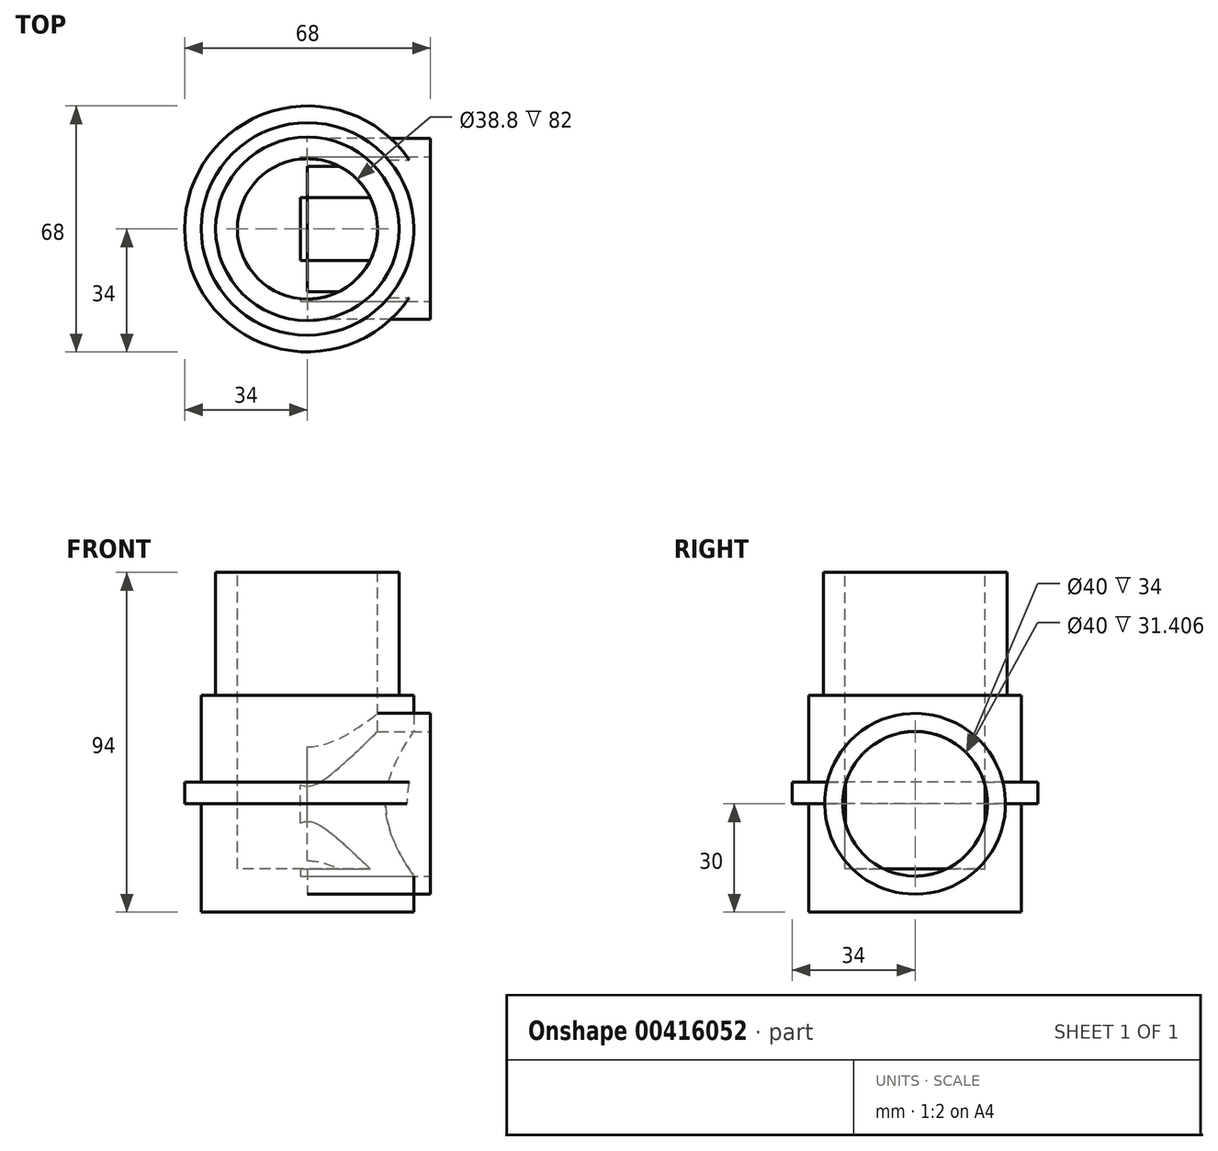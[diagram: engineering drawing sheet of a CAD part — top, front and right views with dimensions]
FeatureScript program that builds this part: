
annotation { "Feature Type Name" : "Feature", "Feature Type Description" : "" }
export const myFeature = defineFeature(function(context is Context, id is Id, definition is map)
    precondition{}
    {
        {
            var Q0;
            Q0=qCreatedBy(makeId("Top.planeOp"),FACE);
            var sketch = newSketch(context, id + "F0", { "sketchPlane" : qUnion([Q0])});
            skCircle(sketch, "E0", {"center": v(0, 0) * mm, "radius": 20.4 * mm});
            skCircle(sketch, "E1", {"center": v(0, 0) * mm, "radius": 34 * mm});
            skSolve(sketch);
        }
        {
            var Q0;
            Q0=makeQuery(id+"F0.imprint","IMPRINT",FACE,{"disambiguationData":[TD([[makeQuery(id+"F0.imprint","IMPRINT",EDGE,{"derivedFrom":sQuery(id+"F0.wireOp",EDGE,"bOa9IgKr-D7bf-5bRc-FIO3-sv5EpX4lF2sY")}),-1.0]])]});
            var Q1;
            Q1=makeQuery(id+"F0.imprint","IMPRINT",FACE,{"disambiguationData":[TD([[makeQuery(id+"F0.imprint","IMPRINT",EDGE,{"derivedFrom":sQuery(id+"F0.wireOp",EDGE,"E0")}),-1.0]])]});
            extrude(context, id + "F1", {"entities" : qUnion([Q0, Q1]), "depth" : 6 * mm, "offsetDistance" : 25 * mm});
        }
        {
            var Q0;
            Q0=makeQuery(id+"F1.opExtrude","CAP_FACE",FACE,{"disambiguationData":[OSD([sQuery(id+"F0.wireOp",EDGE,"E0"),sQuery(id+"F0.wireOp",EDGE,"E1")])],"isStart":false});
            var sketch = newSketch(context, id + "F2", { "sketchPlane" : qUnion([Q0])});
            skCircle(sketch, "E2", {"center": v(0, 0) * mm, "radius": 25.4 * mm});
            skSolve(sketch);
        }
        {
            var Q0;
            Q0=makeQuery(id+"F2.imprint","IMPRINT",FACE,{"disambiguationData":[TD([[makeQuery(id+"F2.imprint","IMPRINT",EDGE,{"derivedFrom":sQuery(id+"F2.wireOp",EDGE,"E2")}),1.0]])]});
            extrude(context, id + "F3", {"entities" : qUnion([Q0]), "operationType" : NewBodyOperationType.ADD, "depth" : 34 * mm, "offsetDistance" : 25 * mm});
        }
        {
            var Q0;
            Q0=qCreatedBy(makeId("Top.planeOp"),FACE);
            var sketch = newSketch(context, id + "F4", { "sketchPlane" : qUnion([Q0])});
            skCircle(sketch, "E3", {"center": v(0, 0) * mm, "radius": 29.4 * mm});
            skSolve(sketch);
        }
        {
            var Q0;
            Q0=makeQuery(id+"F4.imprint","IMPRINT",FACE,{"disambiguationData":[TD([[makeQuery(id+"F4.imprint","IMPRINT",EDGE,{"derivedFrom":sQuery(id+"F4.wireOp",EDGE,"E3")}),1.0]])]});
            extrude(context, id + "F5", {"entities" : qUnion([Q0]), "depth" : 60 * mm, "offsetDistance" : 25 * mm, "symmetric" : true});
        }
        {
            var Q0;
            Q0=qCreatedBy(makeId("Right.planeOp"),FACE);
            var sketch = newSketch(context, id + "F6", { "sketchPlane" : qUnion([Q0])});
            skCircle(sketch, "E4", {"center": v(0, 0) * mm, "radius": 25 * mm});
            skSolve(sketch);
        }
        {
            var Q0;
            Q0 = qSketchRegion(id + "F6", true);
            extrude(context, id + "F7", {"entities" : qUnion([Q0]), "depth" : 34 * mm, "offsetDistance" : 25 * mm});
        }
        {
            var Q0;
            Q0=makeQuery(id+"F7.opExtrude","CAP_FACE",FACE,{"disambiguationData":[OSD([sQuery(id+"F6.wireOp",EDGE,"E4")])],"isStart":false});
            var sketch = newSketch(context, id + "F8", { "sketchPlane" : qUnion([Q0])});
            skCircle(sketch, "E5", {"center": v(0, 0) * mm, "radius": 20 * mm});
            skSolve(sketch);
        }
        {
            var Q0;
            Q0=makeQuery(id+"F8.imprint","IMPRINT",FACE,{"disambiguationData":[TD([[makeQuery(id+"F8.imprint","IMPRINT",EDGE,{"derivedFrom":sQuery(id+"F8.wireOp",EDGE,"E5")}),1.0]])]});
            extrude(context, id + "F9", {"entities" : qUnion([Q0]), "operationType" : NewBodyOperationType.REMOVE, "oppositeDirection" : true, "depth" : 36 * mm, "offsetDistance" : 25 * mm});
        }
        {
            var Q0;
            Q0=makeQuery(id+"F5.opExtrude","CAP_FACE",FACE,{"disambiguationData":[OSD([sQuery(id+"F4.wireOp",EDGE,"E3")])],"isStart":false});
            var sketch = newSketch(context, id + "F10", { "sketchPlane" : qUnion([Q0])});
            skCircle(sketch, "E6", {"center": v(0, 0) * mm, "radius": 25.4 * mm});
            skSolve(sketch);
        }
        {
            var Q0;
            Q0=makeQuery(id+"F10.imprint","IMPRINT",FACE,{"disambiguationData":[TD([[makeQuery(id+"F10.imprint","IMPRINT",EDGE,{"derivedFrom":sQuery(id+"F10.wireOp",EDGE,"E6")}),1.0]])]});
            extrude(context, id + "F11", {"entities" : qUnion([Q0]), "operationType" : NewBodyOperationType.ADD, "depth" : 34 * mm, "offsetDistance" : 25 * mm});
        }
        {
            var Q0;
            Q0=makeQuery(id+"F11.opExtrude","CAP_FACE",FACE,{"disambiguationData":[OSD([sQuery(id+"F10.wireOp",EDGE,"E6")])],"isStart":false});
            var sketch = newSketch(context, id + "F12", { "sketchPlane" : qUnion([Q0])});
            skCircle(sketch, "E7", {"center": v(0, 0) * mm, "radius": 19.4 * mm});
            skSolve(sketch);
        }
        {
            var Q0;
            Q0=makeQuery(id+"F12.imprint","IMPRINT",FACE,{"disambiguationData":[TD([[makeQuery(id+"F12.imprint","IMPRINT",EDGE,{"derivedFrom":sQuery(id+"F12.wireOp",EDGE,"E7")}),1.0]])]});
            extrude(context, id + "F13", {"entities" : qUnion([Q0]), "operationType" : NewBodyOperationType.REMOVE, "oppositeDirection" : true, "depth" : 82 * mm, "offsetDistance" : 25 * mm});
        }
    });
